# Revit family: SCOD
name_source: partatom
category: Lighting Fixtures
revit_build: Autodesk Revit 2014 (Build: 20130308_1515(x64)
units: mm (PartAtom-declared; Revit-internal decimal feet)

## types (1)
- SCOD
    Apparent Load = 78 VA
    Assembly Code = D5020200
    Color Filter = 16777215
    Connector Description = Lighting Connector
    Default Elevation = 1219.2 mm  [stored 4 ft]
    Description = The ScotiaEx is a low energy floodlight with an instant on output delivering 110,000 maintenance free hours at 25 °C. Its excellent temperature range of -50°C to +55°C makes it a global lighting solution providing high output lighting at extreme temperatures.
    Dimming Lamp Color Temperature Shift = <None>
    Emit Shape Visible in Rendering = No
    Emit from Rectangle Length = 150 mm  [stored 0.492126 ft]
    Emit from Rectangle Width = 250 mm  [stored 0.82021 ft]
    Features = Instant on crisp white light output.
Highly Energy Efficient.
110,000 maintenance free hours at 25°C.
Lower power consumption than HID lamps.
Low temperature applications to -50°C.
Crane Damper Bracket available
    Fixture distribution = Direct
    Glass = Hubbell - Glass
    Height = 535 mm
    Housing Material = Paint - Hubbell - Light Silver
    IP Rating = IP66/67
    Lamp = LED
    Length = 444 mm  [stored 1.45669 ft]
    Load Classification = Lighting
    Manufacturer = Chalmit
    Model = SCOD
    Mounting = Paint - Hubbell - Light Silver
    Photometric Web File = SCOD_07L_LE.ies
    Power Factor = 1
    Product Documentation Link = https://hubbellcdn.com
    Product Link = https://www.hubbell.com
    Reflector Finish = Hubbell - White Glass
    Tilt Angle = 90.00°
    URL = https://www.hubbell.com
    Voltage = 120 V
    Warranty = 5 years Warranty
    Wattage Comments = 78W
    Watts = 78 W
    Width = 280 mm  [stored 0.918635 ft]
    Wings = Paint - Hubbell - Light Silver

note: [stored X ft] marks values corroborated as IEEE doubles in the binary element streams (Revit-internal decimal feet)

## geometry (parser evidence)
native form markers: Sweep x2
no freeform markers — native parametric forms only
